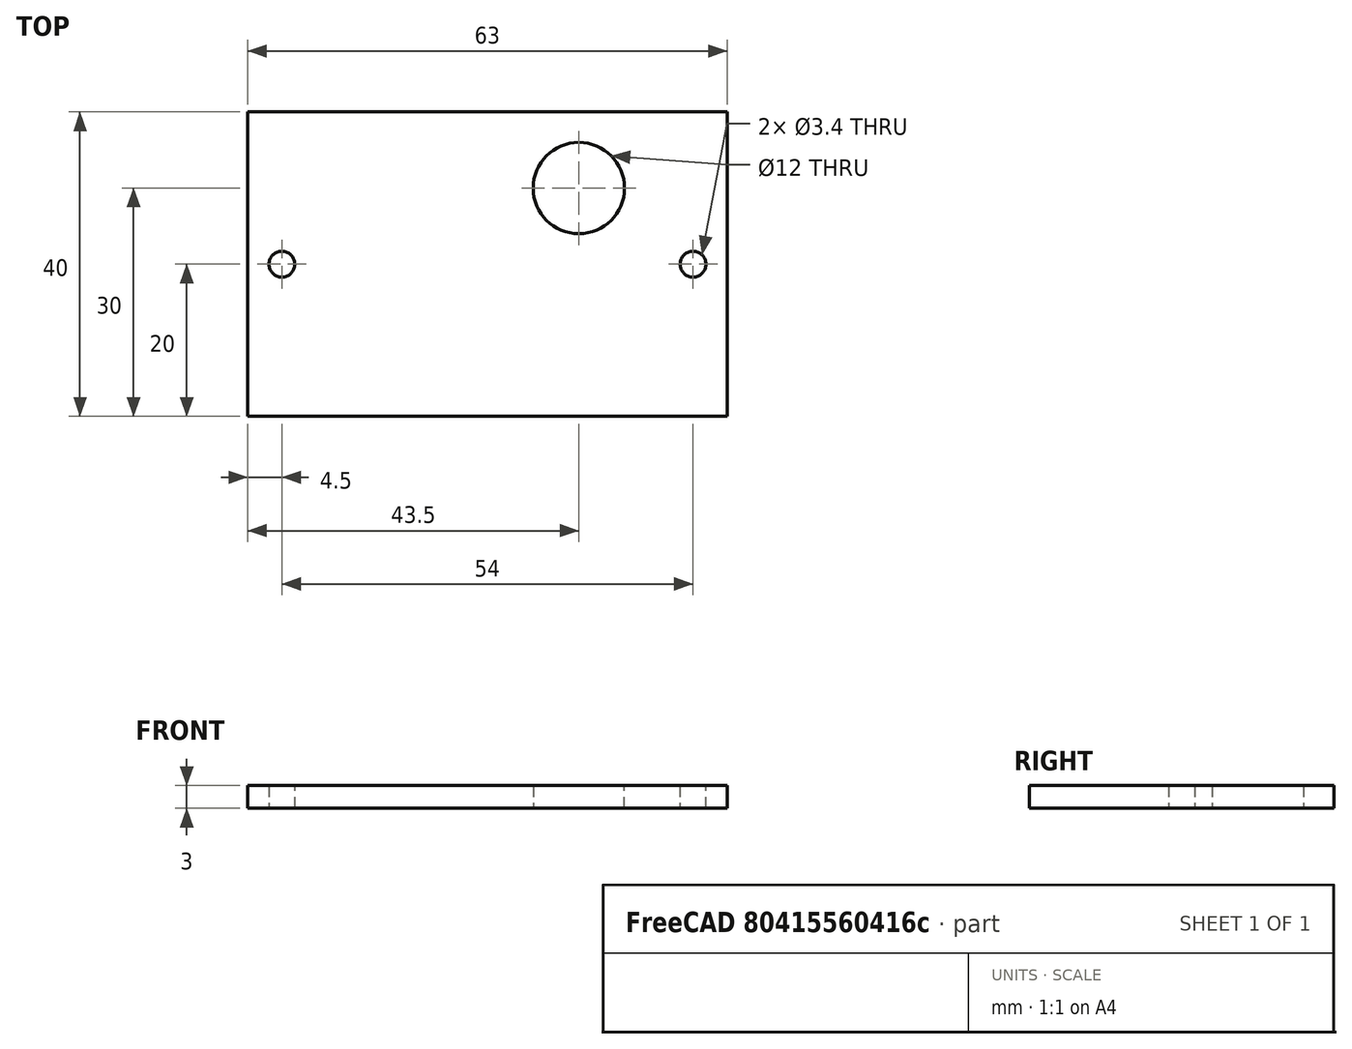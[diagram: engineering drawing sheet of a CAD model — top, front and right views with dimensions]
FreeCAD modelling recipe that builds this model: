
FCSTD DOCUMENT  (FreeCAD 0.17R13522 (Git))
Label: Frente
License: All rights reserved
LicenseURL: http://en.wikipedia.org/wiki/All_rights_reserved
objects: App::Part×1, Sketcher::SketchObject×1, PartDesign::Pad×1, PartDesign::Body×1
note: 4 computed .brp shape members not serialized (recipe doc carries the construction recipe); baked Part::Feature solids carry a one-line shape summary decoded from their .brp

FEATURE [App::Part] Part
  License = CC BY 3.0
  LicenseURL = http://creativecommons.org/licenses/by/3.0/
  Origin = -> Origin
FEATURE [Sketcher::SketchObject] Sketch
  MapMode = 5
  Support = -> [XY_Plane001]
  sketch-geometry (8):
    g0: LineSegment StartX=-31.5 StartY=40 StartZ=0 EndX=31.5 EndY=40 EndZ=0
    g1: LineSegment StartX=31.5 StartY=40 StartZ=0 EndX=31.5 EndY=0 EndZ=0
    g2: LineSegment StartX=31.5 StartY=0 StartZ=0 EndX=-31.5 EndY=0 EndZ=0
    g3: LineSegment StartX=-31.5 StartY=0 StartZ=0 EndX=-31.5 EndY=40 EndZ=0
    g4: Circle CenterX=-27 CenterY=20 CenterZ=0 NormalX=0 NormalY=0 NormalZ=1 AngleXU=0 Radius=1.7
    g5: Circle CenterX=27 CenterY=20 CenterZ=0 NormalX=0 NormalY=0 NormalZ=1 AngleXU=0 Radius=1.7
    g6: Circle CenterX=12 CenterY=30 CenterZ=0 NormalX=0 NormalY=0 NormalZ=1 AngleXU=0 Radius=6
    g7: LineSegment [constr] StartX=-27 StartY=20 StartZ=0 EndX=27 EndY=20 EndZ=0
  constraints (20):
    c: Coincident(g0,g1)
    c: Coincident(g1,g2)
    c: Coincident(g2,g3)
    c: Coincident(g3,g0)
    c: Horizontal(g0)
    c: Horizontal(g2)
    c: Vertical(g1)
    c: Vertical(g3)
    c: DistanceY(g3,g3) = 40
    c: DistanceX(g0,g0) = 63
    c: Symmetric(g2,g1,g-1)
    c: Radius(g5) = 1.7
    c: Equal(g5,g4)
    c: Radius(g6) = 6
    c: Horizontal(g7)
    c: Symmetric(g7,g7,g-2)
    c: Coincident(g4,g7)
    c: Coincident(g5,g7)
    c: DistanceY(g1,g5) = 20
    c: DistanceX(g7,g7) = 54
FEATURE [PartDesign::Pad] Pad
  Length = 3
  Length2 = 100
  Profile = -> Sketch
  Type = 0
FEATURE [PartDesign::Body] Body
  Group = -> [Sketch,Pad]
  Origin = -> Origin001
  Tip = -> Pad
